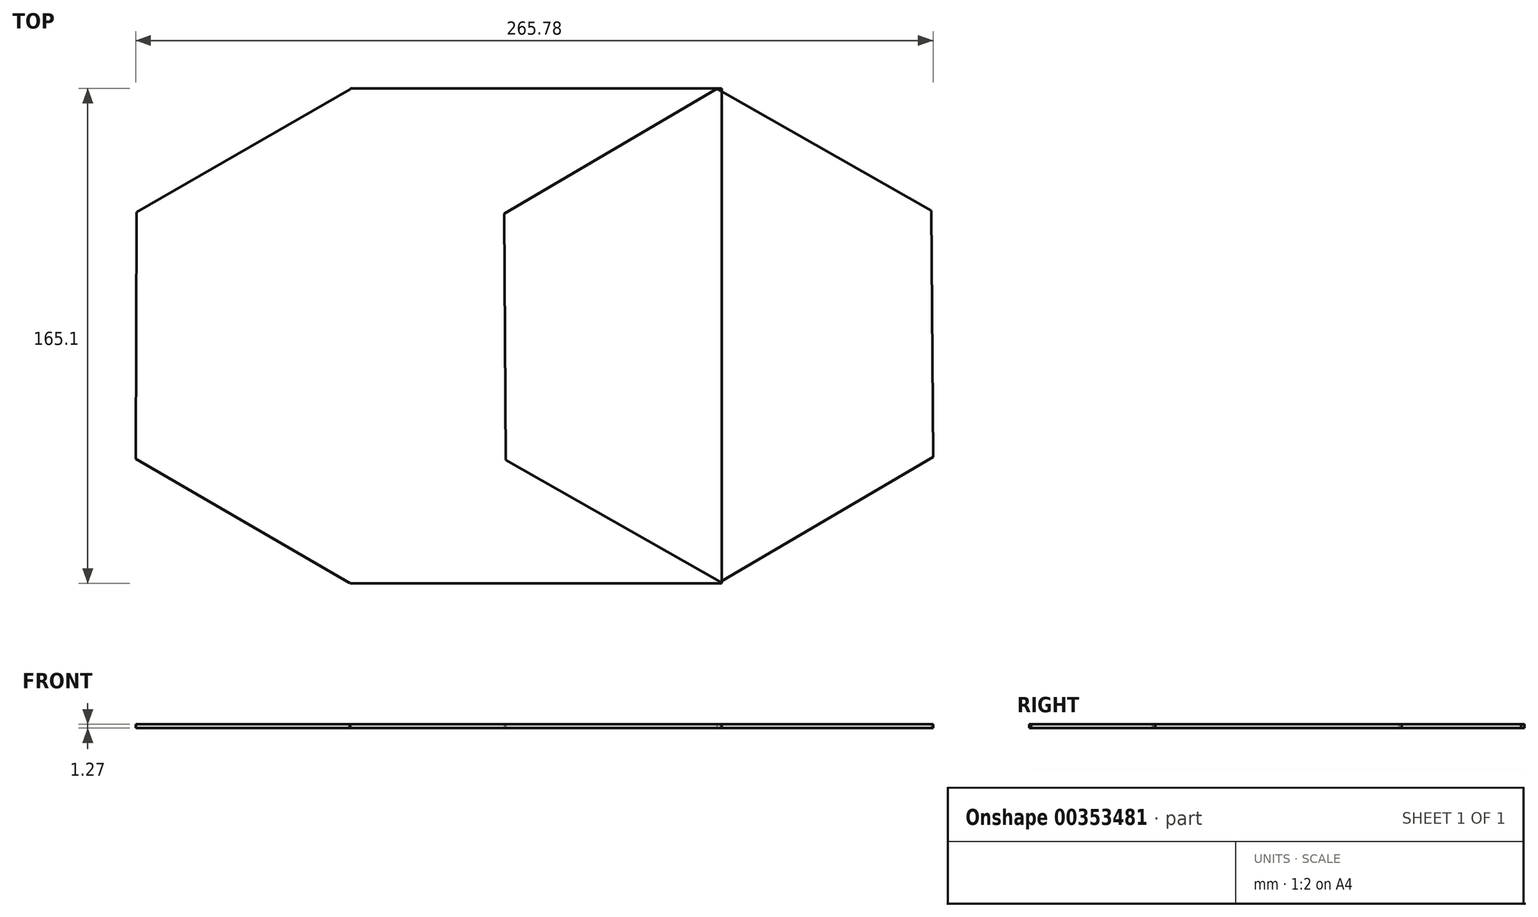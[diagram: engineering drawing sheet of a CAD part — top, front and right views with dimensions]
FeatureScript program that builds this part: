
annotation { "Feature Type Name" : "Feature", "Feature Type Description" : "" }
export const myFeature = defineFeature(function(context is Context, id is Id, definition is map)
    precondition{}
    {
        {
            var Q0;
            Q0=qCreatedBy(makeId("Top.planeOp"),FACE);
            var sketch = newSketch(context, id + "F0", { "sketchPlane" : qUnion([Q0])});
            skLineSegment(sketch, "E0.bottom", {"start": v(0, 0) * mm, "end": v(123.83, 0) * mm});
            skLineSegment(sketch, "E0.top", {"start": v(0, -165.1) * mm, "end": v(123.83, -165.1) * mm});
            skLineSegment(sketch, "E0.left", {"start": v(0, 0) * mm, "end": v(0, -165.1) * mm});
            skLineSegment(sketch, "E0.right", {"start": v(123.83, 0) * mm, "end": v(123.83, -165.1) * mm});
            skSolve(sketch);
        }
        {
            var Q0;
            Q0=makeQuery(id+"F0.imprint","IMPRINT",FACE,{"disambiguationData":[TD([[makeQuery(id+"F0.imprint","IMPRINT",EDGE,{"derivedFrom":sQuery(id+"F0.wireOp",EDGE,"E0.bottom")}),-1.0]])]});
            var sketch = newSketch(context, id + "F1", { "sketchPlane" : qUnion([Q0])});
            skCircle(sketch, "E1.cCircle", {"center": v(0, -82.62) * mm, "radius": 71.38 * mm, "construction": true});
            skLineSegment(sketch, "E1.0", {"start": v(-71.27, -41.23) * mm, "end": v(0.2, -0.2) * mm});
            skLineSegment(sketch, "E1.1", {"start": v(0.2, -0.2) * mm, "end": v(71.48, -41.59) * mm});
            skLineSegment(sketch, "E1.2", {"start": v(71.48, -41.59) * mm, "end": v(71.27, -124) * mm});
            skLineSegment(sketch, "E1.3", {"start": v(71.27, -124) * mm, "end": v(-0.2, -165.03) * mm});
            skLineSegment(sketch, "E1.4", {"start": v(-0.2, -165.03) * mm, "end": v(-71.48, -123.65) * mm});
            skLineSegment(sketch, "E1.5", {"start": v(-71.48, -123.65) * mm, "end": v(-71.27, -41.23) * mm});
            skPoint(sketch, "E1.0.midPoint", {"position": v(-35.53, -20.71) * mm});
            skSolve(sketch);
        }
        {
            var Q0;
            {var subQ1=sQuery(id+"F1.wireOp",EDGE,"E1.4");Q0=makeQuery(id+"F1.imprint","IMPRINT",FACE,{"disambiguationData":[TD([[makeQuery(id+"F1.imprint","IMPRINT",EDGE,{"derivedFrom":subQ1}),-1.0]])]});}
            extrude(context, id + "F2", {"entities" : qUnion([Q0]), "depth" : 1.27 * mm});
        }
        {
            var Q0;
            Q0=makeQuery(id+"F0.imprint","IMPRINT",FACE,{"disambiguationData":[TD([[makeQuery(id+"F0.imprint","IMPRINT",EDGE,{"derivedFrom":sQuery(id+"F0.wireOp",EDGE,"E0.bottom")}),-1.0]])]});
            var sketch = newSketch(context, id + "F3", { "sketchPlane" : qUnion([Q0])});
            skLineSegment(sketch, "E2", {"start": v(122.73, 0) * mm, "end": v(122.73, -82.55) * mm});
            skSolve(sketch);
        }
        {
            var Q0;
            Q0=makeQuery(id+"F3.imprint","IMPRINT",FACE,{"disambiguationData":[TD([[makeQuery(id+"F3.imprint","IMPRINT",EDGE,{"derivedFrom":makeQuery(id+"F0.imprint","IMPRINT",EDGE,{"derivedFrom":sQuery(id+"F0.wireOp",EDGE,"E0.top")})}),1.0]])]});
            var sketch = newSketch(context, id + "F4", { "sketchPlane" : qUnion([Q0])});
            skCircle(sketch, "E3.cCircle", {"center": v(122.8, -82.4) * mm, "radius": 71.2 * mm, "construction": true});
            skLineSegment(sketch, "E3.0", {"start": v(122.22, -0.18) * mm, "end": v(193.72, -40.78) * mm});
            skLineSegment(sketch, "E3.1", {"start": v(193.72, -40.78) * mm, "end": v(194.3, -123) * mm});
            skLineSegment(sketch, "E3.2", {"start": v(194.3, -123) * mm, "end": v(123.39, -164.62) * mm});
            skLineSegment(sketch, "E3.3", {"start": v(123.39, -164.62) * mm, "end": v(51.9, -124.01) * mm});
            skLineSegment(sketch, "E3.4", {"start": v(51.9, -124.01) * mm, "end": v(51.3, -41.8) * mm});
            skLineSegment(sketch, "E3.5", {"start": v(51.3, -41.8) * mm, "end": v(122.22, -0.18) * mm});
            skPoint(sketch, "E3.0.midPoint", {"position": v(157.97, -20.48) * mm});
            skSolve(sketch);
        }
        {
            var Q0;
            {var subQ0=sQuery(id+"F4.wireOp",EDGE,"E3.1");Q0=makeQuery(id+"F4.imprint","IMPRINT",FACE,{"disambiguationData":[TD([[makeQuery(id+"F4.imprint","IMPRINT",EDGE,{"derivedFrom":subQ0}),-1.0]])]});}
            var sketch = newSketch(context, id + "F5", { "sketchPlane" : qUnion([Q0])});
            skLineSegment(sketch, "E4", {"start": v(193.6, -40.39) * mm, "end": v(193.6, -59.44) * mm});
            skSolve(sketch);
        }
        {
            var Q0;
            {var subQ10=sQuery(id+"F4.wireOp",EDGE,"E3.3");Q0=makeQuery(id+"F4.imprint","IMPRINT",FACE,{"disambiguationData":[TD([[makeQuery(id+"F4.imprint","IMPRINT",EDGE,{"derivedFrom":subQ10}),1.0]])]});}
            extrude(context, id + "F6", {"entities" : qUnion([Q0]), "operationType" : NewBodyOperationType.ADD, "depth" : 1.27 * mm});
        }
        {
            var Q0;
            {var subQ0=sQuery(id+"F4.wireOp",EDGE,"E3.1");Q0=makeQuery(id+"F5.imprint","IMPRINT",FACE,{"disambiguationData":[TD([[makeQuery(id+"F5.imprint","IMPRINT",EDGE,{"derivedFrom":makeQuery(id+"F4.imprint","IMPRINT",EDGE,{"derivedFrom":subQ0})}),-1.0]])]});}
            var sketch = newSketch(context, id + "F7", { "sketchPlane" : qUnion([Q0])});
            skLineSegment(sketch, "E5", {"start": v(193.22, -40.7) * mm, "end": v(193.22, -122.08) * mm});
            skSolve(sketch);
        }
        {
            var Q0;
            {var subQ0=sQuery(id+"F4.wireOp",EDGE,"E3.1");Q0=makeQuery(id+"F7.imprint","IMPRINT",FACE,{"disambiguationData":[TD([[makeQuery(id+"F7.imprint","IMPRINT",EDGE,{"derivedFrom":makeQuery(id+"F5.imprint","IMPRINT",EDGE,{"derivedFrom":makeQuery(id+"F4.imprint","IMPRINT",EDGE,{"derivedFrom":subQ0})})}),-1.0]])]});}
            extrude(context, id + "F8", {"entities" : qUnion([Q0]), "depth" : 1.27 * mm});
        }
    });
